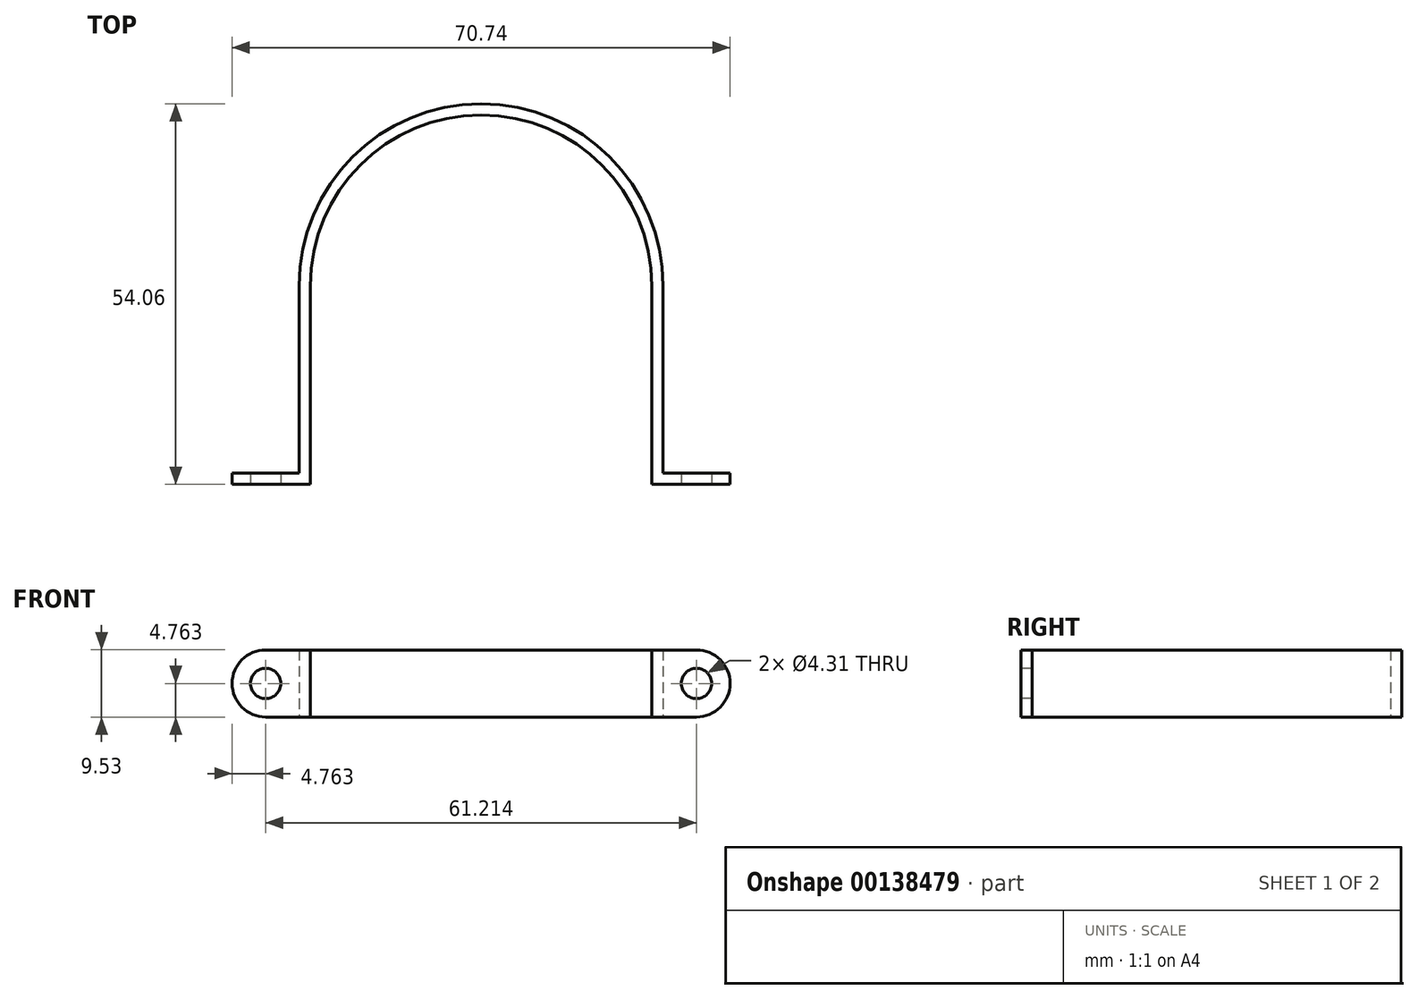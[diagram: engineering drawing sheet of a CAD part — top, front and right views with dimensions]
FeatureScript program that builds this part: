
annotation { "Feature Type Name" : "Feature", "Feature Type Description" : "" }
export const myFeature = defineFeature(function(context is Context, id is Id, definition is map)
    precondition{}
    {
        {
            var Q0;
            Q0=qCreatedBy(makeId("Top.planeOp"),FACE);
            var sketch = newSketch(context, id + "F0", { "sketchPlane" : qUnion([Q0])});
            skLineSegment(sketch, "E0", {"start": v(0, 0) * mm, "end": v(0, -28.22) * mm, "construction": true});
            skLineSegment(sketch, "E1", {"start": v(-24.26, 0) * mm, "end": v(24.26, 0) * mm, "construction": true});
            skLineSegment(sketch, "E2", {"start": v(24.26, 0) * mm, "end": v(25.84, 0) * mm, "construction": true});
            skLineSegment(sketch, "E3", {"start": v(-24.26, 0) * mm, "end": v(-25.84, 0) * mm, "construction": true});
            skLineSegment(sketch, "E4", {"start": v(-24.26, -28.22) * mm, "end": v(24.26, -28.22) * mm, "construction": true});
            skLineSegment(sketch, "E5", {"start": v(-24.26, 0) * mm, "end": v(-24.26, -28.22) * mm});
            skLineSegment(sketch, "E6", {"start": v(-25.84, 0) * mm, "end": v(-25.84, -26.63) * mm});
            skLineSegment(sketch, "E7", {"start": v(-24.26, -28.22) * mm, "end": v(-35.37, -28.22) * mm});
            skLineSegment(sketch, "E8", {"start": v(-35.37, -28.22) * mm, "end": v(-35.37, -26.63) * mm});
            skLineSegment(sketch, "E9", {"start": v(-35.37, -26.63) * mm, "end": v(-25.84, -26.63) * mm});
            skLineSegment(sketch, "E10", {"start": v(24.26, 0) * mm, "end": v(24.26, -28.22) * mm});
            skLineSegment(sketch, "E11", {"start": v(25.84, 0) * mm, "end": v(25.84, -26.63) * mm});
            skLineSegment(sketch, "E12", {"start": v(25.84, -26.63) * mm, "end": v(35.37, -26.63) * mm});
            skLineSegment(sketch, "E13", {"start": v(35.37, -26.63) * mm, "end": v(35.37, -28.22) * mm});
            skLineSegment(sketch, "E14", {"start": v(35.37, -28.22) * mm, "end": v(24.26, -28.22) * mm});
            skArc(sketch, "E15", {"start": v(24.26, 0) * mm, "mid": v(0, 24.26) * mm, "end": v(-24.26, 0) * mm});
            skArc(sketch, "E16", {"start": v(25.84, 0) * mm, "mid": v(0, 25.84) * mm, "end": v(-25.84, 0) * mm});
            skSolve(sketch);
        }
        {
            var Q0;
            Q0 = qSketchRegion(id + "F0", true);
            extrude(context, id + "F1", {"entities" : qUnion([Q0]), "depth" : 9.52 * mm});
        }
        {
            var Q0;
            Q0=makeQuery(id+"F1.opExtrude","CAP_EDGE",EDGE,{"disambiguationData":[OSD([sQuery(id+"F0.wireOp",EDGE,"E13")])],"isStart":false});
            var Q1;
            Q1=makeQuery(id+"F1.opExtrude","CAP_EDGE",EDGE,{"disambiguationData":[OSD([sQuery(id+"F0.wireOp",EDGE,"E13")])],"isStart":true});
            var Q2;
            Q2=makeQuery(id+"F1.opExtrude","CAP_EDGE",EDGE,{"disambiguationData":[OSD([sQuery(id+"F0.wireOp",EDGE,"E8")])],"isStart":true});
            var Q3;
            Q3=makeQuery(id+"F1.opExtrude","CAP_EDGE",EDGE,{"disambiguationData":[OSD([sQuery(id+"F0.wireOp",EDGE,"E8")])],"isStart":false});
            fillet(context, id + "F2", {"entities" : qUnion([Q0, Q1, Q2, Q3]), "radius" : 4.76 * mm, "tangentPropagation" : true, "allowEdgeOverflow" : false});
        }
        {
            var Q0;
            Q0=makeQuery(id+"F1.opExtrude","SWEPT_FACE",FACE,{"disambiguationData":[OSD([sQuery(id+"F0.wireOp",EDGE,"E14")])]});
            var sketch = newSketch(context, id + "F3", { "sketchPlane" : qUnion([Q0])});
            skCircle(sketch, "E17", {"center": v(30.6, 4.76) * mm, "radius": 2.15 * mm});
            skCircle(sketch, "E18", {"center": v(-30.6, 4.76) * mm, "radius": 2.15 * mm});
            skSolve(sketch);
        }
        {
            var Q0;
            Q0 = qSketchRegion(id + "F3", true);
            var Q1;
            Q1=makeQuery(id+"F1.opExtrude","SWEPT_FACE",FACE,{"disambiguationData":[OSD([sQuery(id+"F0.wireOp",EDGE,"E12")])]});
            extrude(context, id + "F4", {"entities" : qUnion([Q0]), "operationType" : NewBodyOperationType.REMOVE, "endBound" : BoundingType.UP_TO_SURFACE, "oppositeDirection" : true, "endBoundEntityFace" : qUnion([Q1]), "depth" : 25.4 * mm});
        }
    });
